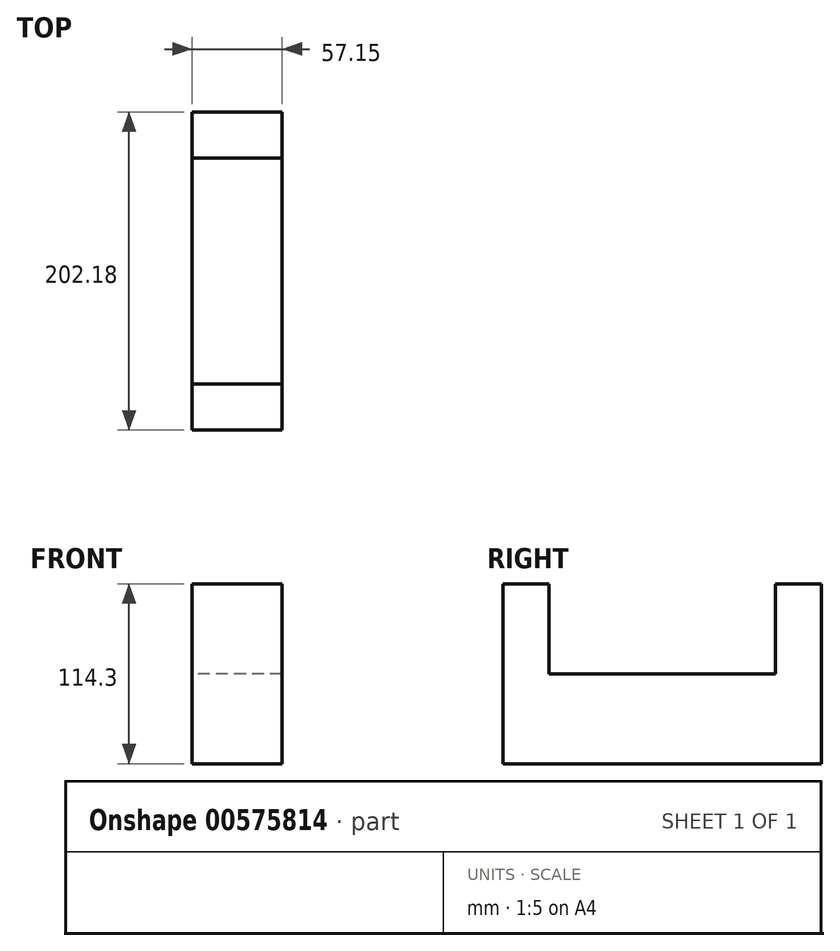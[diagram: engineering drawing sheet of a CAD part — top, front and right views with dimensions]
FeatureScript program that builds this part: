
annotation { "Feature Type Name" : "Feature", "Feature Type Description" : "" }
export const myFeature = defineFeature(function(context is Context, id is Id, definition is map)
    precondition{}
    {
        {
            var Q0;
            Q0=qCreatedBy(makeId("Right.planeOp"),FACE);
            var sketch = newSketch(context, id + "F0", { "sketchPlane" : qUnion([Q0])});
            skLineSegment(sketch, "E0.bottom", {"start": v(-29.21, 10.9) * mm, "end": v(172.97, 10.9) * mm});
            skLineSegment(sketch, "E0.top", {"start": v(-29.2, -46.24) * mm, "end": v(172.97, -46.24) * mm});
            skLineSegment(sketch, "E0.left", {"start": v(-29.2, 10.9) * mm, "end": v(-29.2, -46.24) * mm});
            skLineSegment(sketch, "E0.right", {"start": v(172.97, 10.9) * mm, "end": v(172.97, -46.24) * mm});
            skLineSegment(sketch, "E1.bottom", {"start": v(-29.21, 68.06) * mm, "end": v(0, 68.06) * mm});
            skLineSegment(sketch, "E1.top", {"start": v(-29.2, -46.24) * mm, "end": v(0, -46.24) * mm});
            skLineSegment(sketch, "E1.left", {"start": v(-29.21, 68.06) * mm, "end": v(-29.2, -46.24) * mm});
            skLineSegment(sketch, "E1.right", {"start": v(0, 68.06) * mm, "end": v(0, -46.24) * mm});
            skLineSegment(sketch, "E2.bottom", {"start": v(172.97, -46.24) * mm, "end": v(143.76, -46.24) * mm});
            skLineSegment(sketch, "E2.top", {"start": v(172.97, 68.06) * mm, "end": v(143.76, 68.06) * mm});
            skLineSegment(sketch, "E2.left", {"start": v(172.97, -46.24) * mm, "end": v(172.97, 68.06) * mm});
            skLineSegment(sketch, "E2.right", {"start": v(143.76, -46.24) * mm, "end": v(143.76, 68.06) * mm});
            skSolve(sketch);
        }
        {
            var Q0;
            {var subQ5=sQuery(id+"F0.wireOp",EDGE,"E2.top");Q0=makeQuery(id+"F0.imprint","IMPRINT",FACE,{"disambiguationData":[TD([[makeQuery(id+"F0.imprint","IMPRINT",EDGE,{"derivedFrom":subQ5}),1.0]])]});}
            var Q1;
            {var subQ5=sQuery(id+"F0.wireOp",EDGE,"E2.bottom");Q1=makeQuery(id+"F0.imprint","IMPRINT",FACE,{"disambiguationData":[TD([[makeQuery(id+"F0.imprint","IMPRINT",EDGE,{"derivedFrom":subQ5}),-1.0]])]});}
            var Q2;
            {var subQ5=sQuery(id+"F0.wireOp",EDGE,"E0.top");Q2=makeQuery(id+"F0.imprint","IMPRINT",FACE,{"disambiguationData":[TD([[makeQuery(id+"F0.imprint","IMPRINT",EDGE,{"derivedFrom":subQ5}),1.0]])]});}
            var Q3;
            {var subQ5=sQuery(id+"F0.wireOp",EDGE,"E1.top");Q3=makeQuery(id+"F0.imprint","IMPRINT",FACE,{"disambiguationData":[TD([[makeQuery(id+"F0.imprint","IMPRINT",EDGE,{"derivedFrom":subQ5}),1.0]])]});}
            var Q4;
            {var subQ5=sQuery(id+"F0.wireOp",EDGE,"E1.bottom");Q4=makeQuery(id+"F0.imprint","IMPRINT",FACE,{"disambiguationData":[TD([[makeQuery(id+"F0.imprint","IMPRINT",EDGE,{"derivedFrom":subQ5}),-1.0]])]});}
            extrude(context, id + "F1", {"entities" : qUnion([Q0, Q1, Q2, Q3, Q4]), "depth" : 57.15 * mm, "offsetDistance" : 25.4 * mm});
        }
    });
